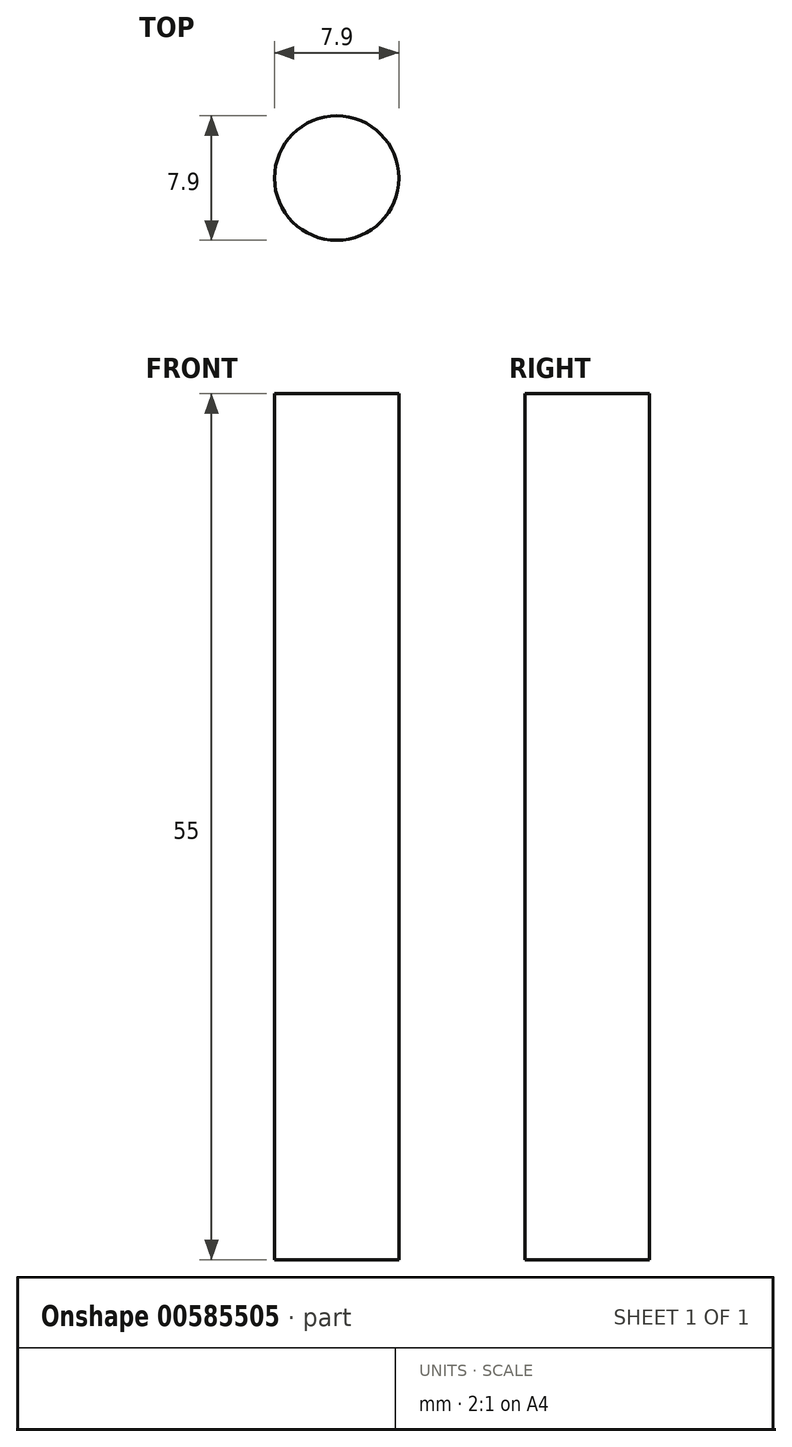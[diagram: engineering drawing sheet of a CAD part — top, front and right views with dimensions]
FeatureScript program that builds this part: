
annotation { "Feature Type Name" : "Feature", "Feature Type Description" : "" }
export const myFeature = defineFeature(function(context is Context, id is Id, definition is map)
    precondition{}
    {
        {
            var Q0;
            Q0=qCreatedBy(makeId("Top.planeOp"),FACE);
            var sketch = newSketch(context, id + "F0", { "sketchPlane" : qUnion([Q0])});
            skCircle(sketch, "E0", {"center": v(0, 0) * mm, "radius": 3.95 * mm});
            skSolve(sketch);
        }
        {
            var Q0;
            Q0 = qSketchRegion(id + "F0", true);
            extrude(context, id + "F1", {"entities" : qUnion([Q0]), "depth" : 55 * mm, "offsetDistance" : 25 * mm});
        }
    });
